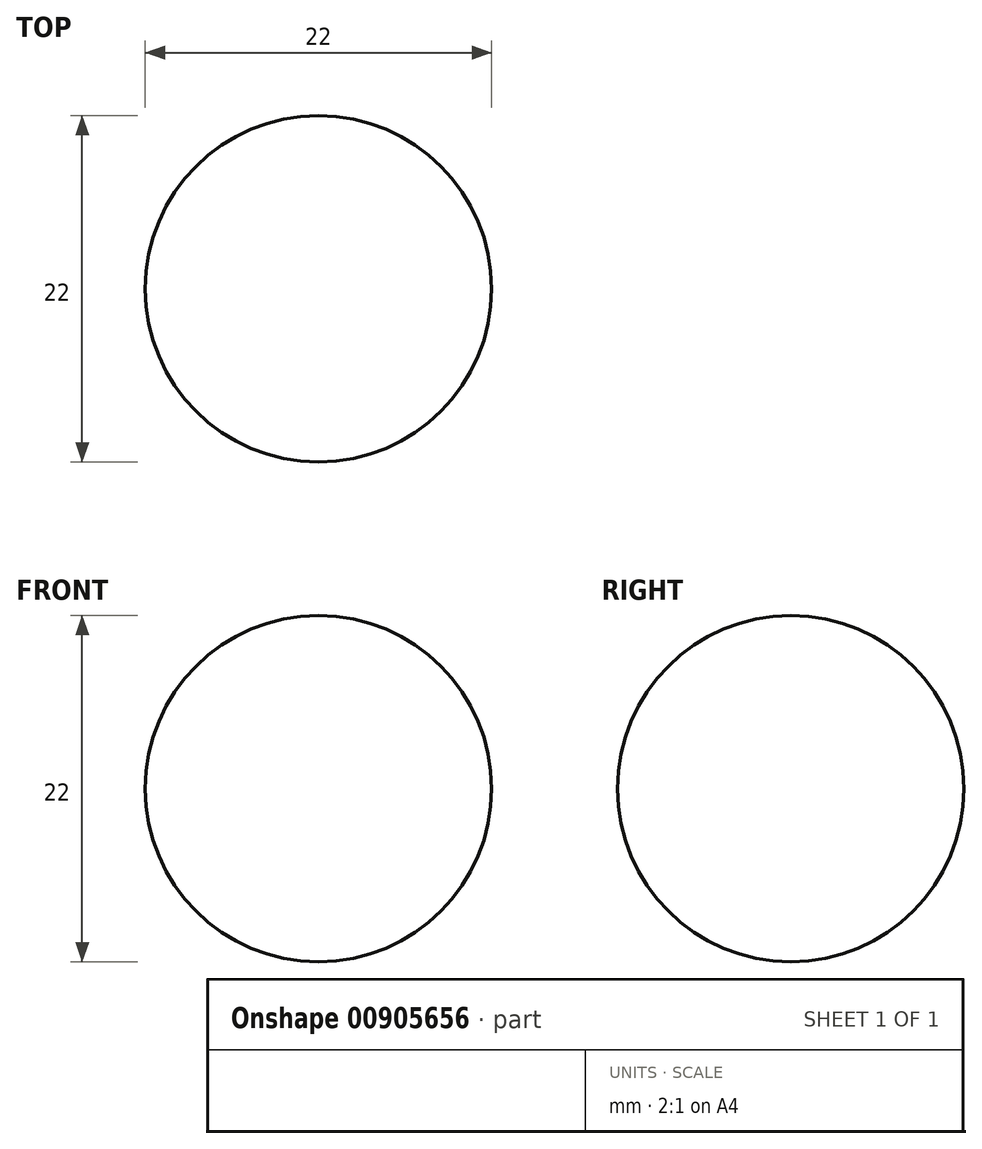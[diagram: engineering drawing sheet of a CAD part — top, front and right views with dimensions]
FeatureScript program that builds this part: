
annotation { "Feature Type Name" : "Feature", "Feature Type Description" : "" }
export const myFeature = defineFeature(function(context is Context, id is Id, definition is map)
    precondition{}
    {
        {
            var Q0;
            Q0=qCreatedBy(makeId("Front.planeOp"),FACE);
            var sketch = newSketch(context, id + "F0", { "sketchPlane" : qUnion([Q0])});
            skCircle(sketch, "E0", {"center": v(0, 0) * mm, "radius": 11 * mm});
            skLineSegment(sketch, "E1", {"start": v(-23.74, 0) * mm, "end": v(33.6, 0) * mm});
            skSolve(sketch);
        }
        {
            var Q0;
            {var subQ0=sQuery(id+"F0.wireOp",EDGE,"E1");var subQ1=sQuery(id+"F0.wireOp",EDGE,"E0");var subQ2=makeQuery(id+"F0.imprint","INTERSECT",VERTEX,{"disambiguationData":[OD(0.0)],"derivedFrom":[subQ1,subQ0]});Q0=makeQuery(id+"F0.imprint","IMPRINT",FACE,{"disambiguationData":[TD([[makeQuery(id+"F0.imprint","IMPRINT",EDGE,{"disambiguationData":[TD([[subQ2,-1.0]])],"derivedFrom":subQ1}),1.0]])]});}
            var Q1;
            Q1=sQuery(id+"F0.wireOp",EDGE,"E1");
            revolve(context, id + "F1", {"surfaceOperationType" : NewSurfaceOperationType.NEW, "entities" : qUnion([Q0]), "axis" : qUnion([Q1]), "revolveType" : RevolveType.FULL});
        }
    });
